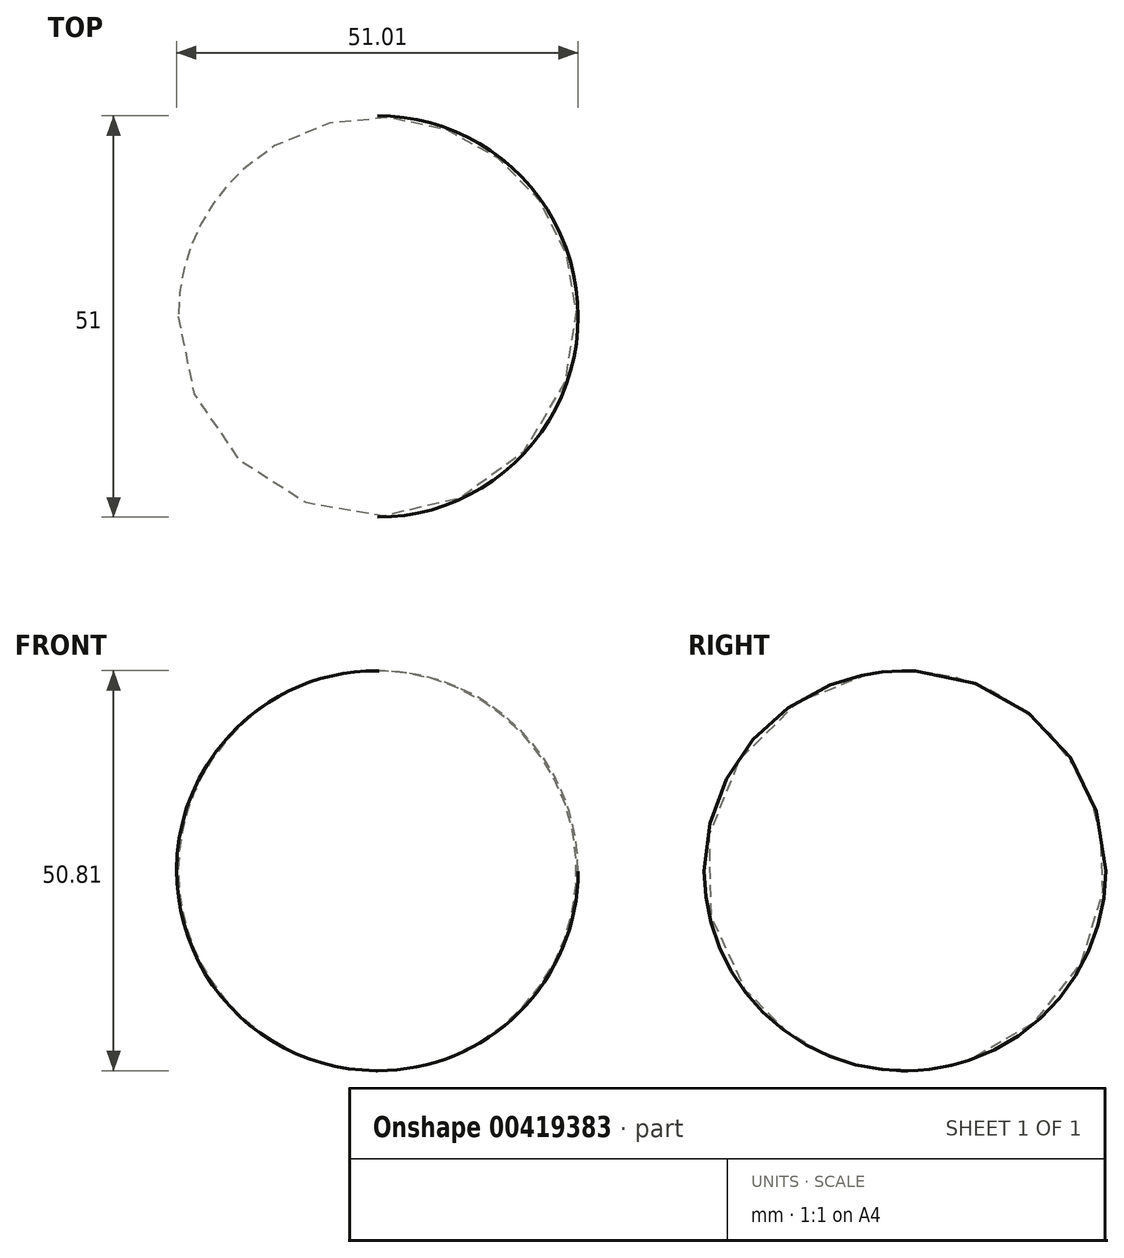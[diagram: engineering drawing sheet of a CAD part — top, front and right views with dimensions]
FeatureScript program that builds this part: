
annotation { "Feature Type Name" : "Feature", "Feature Type Description" : "" }
export const myFeature = defineFeature(function(context is Context, id is Id, definition is map)
    precondition{}
    {
        {
            var Q0;
            Q0=qCreatedBy(makeId("Front.planeOp"),FACE);
            var sketch = newSketch(context, id + "F0", { "sketchPlane" : qUnion([Q0])});
            skArc(sketch, "E0", {"start": v(-37.65, 64.17) * mm, "mid": v(-63.25, 38.87) * mm, "end": v(-37.84, 13.38) * mm});
            skLineSegment(sketch, "E1", {"start": v(-37.65, 64.17) * mm, "end": v(-37.85, 11.85) * mm});
            skSolve(sketch);
        }
        {
            var Q0;
            {var subQ0=sQuery(id+"F0.wireOp",EDGE,"E0");Q0=makeQuery(id+"F0.imprint","IMPRINT",FACE,{"disambiguationData":[TD([[makeQuery(id+"F0.imprint","IMPRINT",EDGE,{"derivedFrom":subQ0}),1.0]])]});}
            var Q1;
            Q1=sQuery(id+"F0.wireOp",EDGE,"E1");
            revolve(context, id + "F1", {"entities" : qUnion([Q0]), "axis" : qUnion([Q1]), "revolveType" : RevolveType.FULL});
        }
    });
